# Revit family: TD92_MES339_ROS060_RVT20_R00
name_source: partatom
category: Mobiliário
units: mm (PartAtom-declared; Revit-internal decimal feet)

## family parameters
Com base no plano de trabalho = Não
Compartilhado = Não
Corte com vazios quando carregada = Não
Número OmniClass = 23.40.20.00
Ponto de cálculo do ambiente = Não
Sempre na vertical = Sim
Título OmniClass = General Furniture and Specialties

## types (1)
- TD92_MES339_ROS060_RVT20_R00
    Descrição = As crianças precisam de ambientes coloridos para expandir seu imaginário e criatividade. Por isso, uma excelente escolha para equipar o quarto ou o ambiente de aprendizado e brincadeira dos pequenos é a Mesa Tramontina Sofia Infantil em Polipropileno e Fibra de Vidro. Ela conta com formato triangular, diferenciando-se das mesas infantis tradicionais. Com ela, você poderá criar diversas composições e formatos se utilizar mais de uma das mesas da linha, variando conforme a atividade proposta. Seu design é diferenciado e sua cor super vibrante, características que vão chamar a atenção dos pequenos e deixá-los muito mais espertos. Ela ainda possui um dispositivo de conexão fixado na área rebaixada do tampo, garantindo a segurança e a comodidade na hora da brincadeira e do aprendizado. Sem dúvida, o produto perfeito para levar alegria para a criançada!
    Elevação padrão = 0  [stored 0 ft]
    Fabricante = Tramontina Delta S/A
    Modelo = Mesa Infantil Tramontina Sofia em Polipropileno e Fibra de Vidro Rosa
    Nota-chave = 92339060
    URL = https://www.tramontinastore.com

note: [stored X ft] marks values corroborated as IEEE doubles in the binary element streams (Revit-internal decimal feet)
